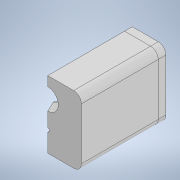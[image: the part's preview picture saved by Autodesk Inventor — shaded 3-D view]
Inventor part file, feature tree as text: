
AUTODESK INVENTOR PART (.ipt)
format: ipt  version: 2022 (Build 260153000, 153)  size: 11,729,408 bytes
history: native  units: mm
features: sketch x5, extrude x4, other x3, direct_edit x1, revolve x1, sweep x1, chamfer x1, plane x1, mirror x1, thicken_offset x1, fillet x1, boolean_combine x1, projected_geometry x1
ambient origin geometry x8: Origin, YZ Plane, XZ Plane, XY Plane, X Axis, Y Axis, Z Axis, Center Point
bodies: Solid1 (feature_tree), Solid2 (feature_tree), Solid3 (feature_tree)
feature tree (22):
  other  "chess_pawn"
  other  "MeshFeature1"
  direct_edit  "Direct Edit1"
  sketch  "Sketch1"  dims[d0=7.8mm d1=10.0mm d2=10.0mm d3=35.0mm]
  extrude  "Extrusion1"  Depth=35.0mm
  revolve  "Revolution1"  [1 undecoded]
  sweep  "Sweep1"
  chamfer  "Chamfer1"  Distance=31.0mm
  plane  "Work Plane1"
  mirror  "Mirror1"
  thicken_offset  "Thicken1"
  extrude  "Extrusion2"  Depth=35.0mm TaperAngle=0.0deg
  extrude  "Extrusion3"  TaperAngle=90.0deg  [1 undecoded]
  fillet  "Fillet1"  Radius=5.0mm
  extrude  "Extrusion4"  TaperAngle=0.0deg  [1 undecoded]
  boolean_combine  "Combine1"
  sketch  "Sketch2"  dims[d5=40.0mm d6=9.5mm]
  sketch  "Sketch3"  dims[d7=3.5mm d8=15.0mm]
  sketch  "Sketch4"  dims[d9=3.0mm]
  sketch  "Sketch5"  dims[d10=13.5mm d11=31.0mm d12=35.0mm d13=0.0mm d14=90.0deg d15=5.0mm d16=0.0mm d17=0.0mm d18=3.0mm d19=2.0mm d20=45.0deg d21=1.5mm d22=1.5mm d23=3.25mm d24=0.0mm d25=3.25mm d26=0.0mm d27=4.0mm d28=0.0mm d29=4.0mm]
  projected_geometry  "Projected Loop1"
  other  "Scale1"
note: 3 required parameter values undecoded (feature->parameter linkage not recoverable at this tier; creation-order binding heuristic only, values carry confidence <= 0.55)